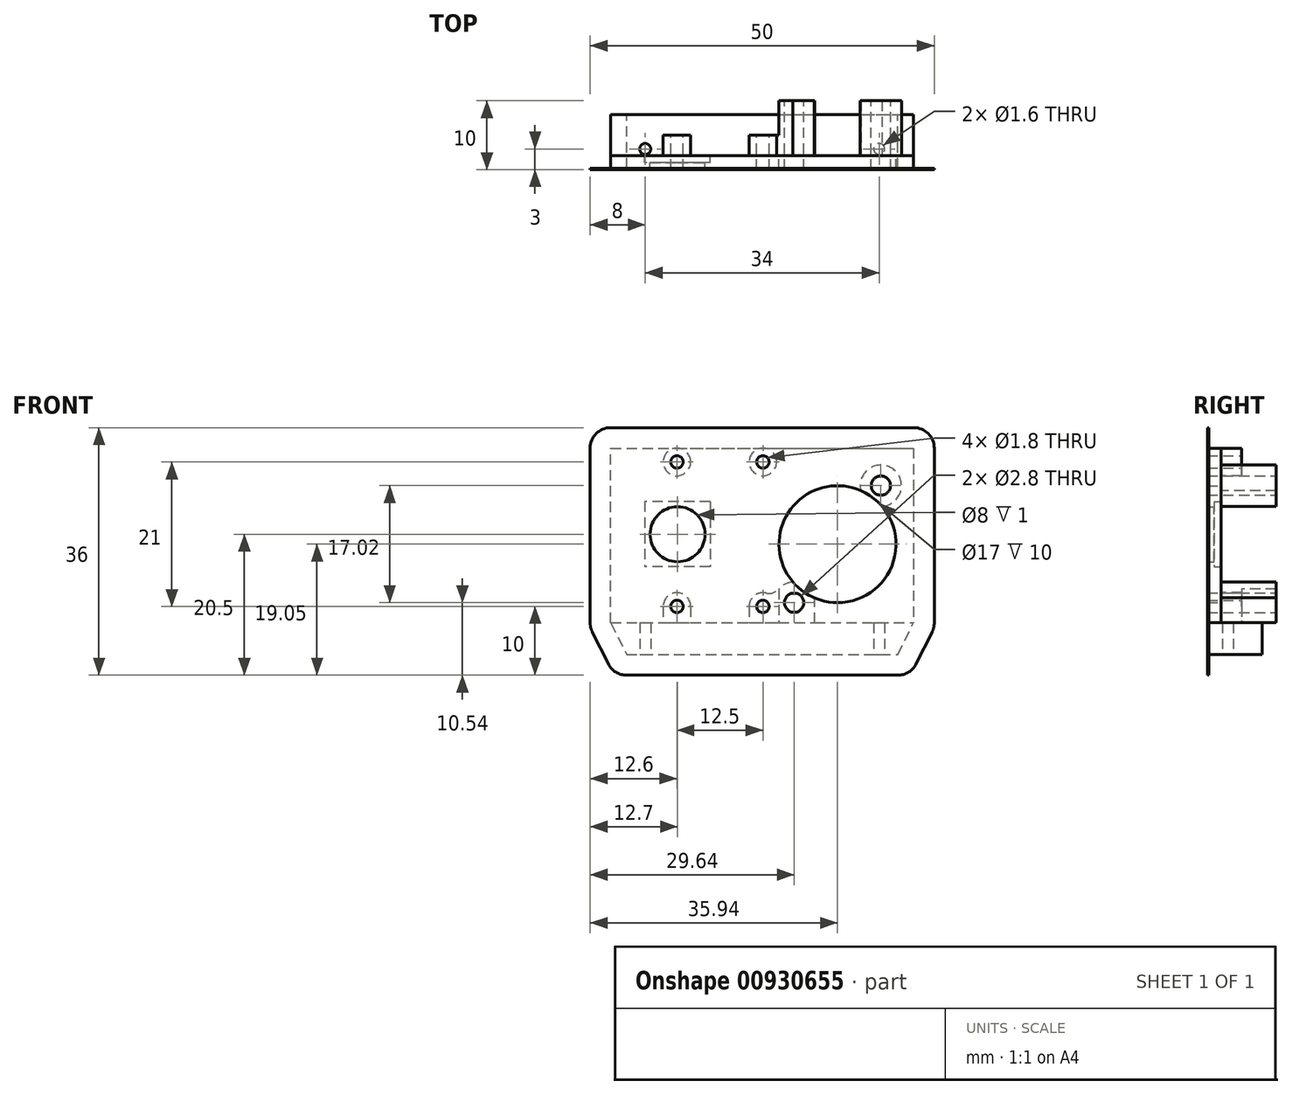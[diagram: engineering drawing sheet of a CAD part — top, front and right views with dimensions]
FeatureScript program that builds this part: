
annotation { "Feature Type Name" : "Feature", "Feature Type Description" : "" }
export const myFeature = defineFeature(function(context is Context, id is Id, definition is map)
    precondition{}
    {
        {
            var Q0;
            Q0=qCreatedBy(makeId("Front.planeOp"),FACE);
            var sketch = newSketch(context, id + "F0", { "sketchPlane" : qUnion([Q0])});
            skLineSegment(sketch, "E0", {"start": v(-22.5, 0) * mm, "end": v(22.5, 0) * mm, "construction": true});
            skLineSegment(sketch, "E1", {"start": v(-20, -5) * mm, "end": v(20, -5) * mm, "construction": true});
            skLineSegment(sketch, "E2", {"start": v(20, -5) * mm, "end": v(22.5, 0) * mm, "construction": true});
            skLineSegment(sketch, "E3", {"start": v(-22.5, 0) * mm, "end": v(-20, -5) * mm, "construction": true});
            skLineSegment(sketch, "E4.bottom", {"start": v(2.1, 22.6) * mm, "end": v(22, 22.6) * mm, "construction": true});
            skLineSegment(sketch, "E4.top", {"start": v(2.1, 0.5) * mm, "end": v(22, 0.5) * mm, "construction": true});
            skLineSegment(sketch, "E4.left", {"start": v(2.1, 22.6) * mm, "end": v(2.1, 0.5) * mm, "construction": true});
            skLineSegment(sketch, "E4.right", {"start": v(22, 22.6) * mm, "end": v(22, 0.5) * mm, "construction": true});
            skLineSegment(sketch, "E5.bottom", {"start": v(-19.76, 25.5) * mm, "end": v(0.1, 25.5) * mm, "construction": true});
            skLineSegment(sketch, "E5.top", {"start": v(-19.76, 0.5) * mm, "end": v(0.1, 0.5) * mm, "construction": true});
            skLineSegment(sketch, "E5.left", {"start": v(-21.76, 23.5) * mm, "end": v(-21.76, 2.5) * mm, "construction": true});
            skLineSegment(sketch, "E5.right", {"start": v(2.1, 23.5) * mm, "end": v(2.1, 2.5) * mm, "construction": true});
            skArc(sketch, "E6", {"start": v(-19.76, 25.5) * mm, "mid": v(-21.18, 24.91) * mm, "end": v(-21.76, 23.5) * mm, "construction": true});
            skArc(sketch, "E7", {"start": v(2.1, 23.5) * mm, "mid": v(1.51, 24.91) * mm, "end": v(0.1, 25.5) * mm, "construction": true});
            skArc(sketch, "E8", {"start": v(-21.76, 2.5) * mm, "mid": v(-21.18, 1.09) * mm, "end": v(-19.76, 0.5) * mm, "construction": true});
            skArc(sketch, "E9", {"start": v(0.1, 0.5) * mm, "mid": v(1.51, 1.09) * mm, "end": v(2.1, 2.5) * mm, "construction": true});
            skCircle(sketch, "E10", {"center": v(-12.4, 23.5) * mm, "radius": 1.1 * mm, "construction": true});
            skCircle(sketch, "E11", {"center": v(-12.4, 2.5) * mm, "radius": 1.1 * mm, "construction": true});
            skCircle(sketch, "E12", {"center": v(0.1, 2.5) * mm, "radius": 1.1 * mm, "construction": true});
            skCircle(sketch, "E13", {"center": v(0.1, 23.5) * mm, "radius": 1.1 * mm, "construction": true});
            skLineSegment(sketch, "E14", {"start": v(-12.4, 23.5) * mm, "end": v(0.1, 23.5) * mm, "construction": true});
            skLineSegment(sketch, "E15", {"start": v(-12.4, 23.5) * mm, "end": v(-12.4, 2.5) * mm, "construction": true});
            skCircle(sketch, "E16", {"center": v(10.94, 11.55) * mm, "radius": 8.2 * mm, "construction": true});
            skCircle(sketch, "E17", {"center": v(17.24, 20.06) * mm, "radius": 1.55 * mm, "construction": true});
            skCircle(sketch, "E18", {"center": v(4.64, 3.04) * mm, "radius": 1.55 * mm, "construction": true});
            skLineSegment(sketch, "E19.bottom", {"start": v(-16.55, 17.25) * mm, "end": v(-8.05, 17.25) * mm, "construction": true});
            skLineSegment(sketch, "E19.top", {"start": v(-16.55, 8.75) * mm, "end": v(-8.05, 8.75) * mm, "construction": true});
            skLineSegment(sketch, "E19.left", {"start": v(-16.55, 17.25) * mm, "end": v(-16.55, 8.75) * mm, "construction": true});
            skLineSegment(sketch, "E19.right", {"start": v(-8.05, 17.25) * mm, "end": v(-8.05, 8.75) * mm, "construction": true});
            skCircle(sketch, "E20", {"center": v(-12.3, 13) * mm, "radius": 3.7 * mm, "construction": true});
            skCircle(sketch, "E21", {"center": v(20.8, 17.44) * mm, "radius": 0.5 * mm, "construction": true});
            skCircle(sketch, "E22", {"center": v(20.8, 14.9) * mm, "radius": 0.5 * mm, "construction": true});
            skLineSegment(sketch, "E23", {"start": v(20.8, 17.44) * mm, "end": v(20.8, 2.2) * mm, "construction": true});
            skCircle(sketch, "E24", {"center": v(20.8, 12.36) * mm, "radius": 0.5 * mm, "construction": true});
            skCircle(sketch, "E25", {"center": v(20.8, 9.82) * mm, "radius": 0.5 * mm, "construction": true});
            skCircle(sketch, "E26", {"center": v(20.8, 7.28) * mm, "radius": 0.5 * mm, "construction": true});
            skCircle(sketch, "E27", {"center": v(20.8, 4.74) * mm, "radius": 0.5 * mm, "construction": true});
            skCircle(sketch, "E28", {"center": v(20.8, 2.2) * mm, "radius": 0.5 * mm, "construction": true});
            skSolve(sketch);
        }
        {
            var Q0;
            Q0=qCreatedBy(makeId("Front.planeOp"),FACE);
            var sketch = newSketch(context, id + "F1", { "sketchPlane" : qUnion([Q0])});
            skLineSegment(sketch, "E29", {"start": v(-22, 0.12) * mm, "end": v(-19.7, -4.5) * mm});
            skLineSegment(sketch, "E30", {"start": v(-19.7, -4.5) * mm, "end": v(19.7, -4.5) * mm});
            skLineSegment(sketch, "E31", {"start": v(19.7, -4.5) * mm, "end": v(22, 0.12) * mm});
            skLineSegment(sketch, "E32", {"start": v(-22, 0.12) * mm, "end": v(-22, 25.5) * mm});
            skLineSegment(sketch, "E33", {"start": v(-22, 25.5) * mm, "end": v(22, 25.5) * mm});
            skLineSegment(sketch, "E34", {"start": v(22, 25.5) * mm, "end": v(22, 0.12) * mm});
            skCircle(sketch, "E35", {"center": v(-12.3, 13) * mm, "radius": 4 * mm});
            skCircle(sketch, "E36", {"center": v(10.94, 11.55) * mm, "radius": 8.5 * mm});
            skSolve(sketch);
        }
        {
            var Q0;
            Q0=qSketchRegion(id+"F1",true);
            extrude(context, id + "F2", {"entities" : qUnion([Q0]), "depth" : 2 * mm, "offsetDistance" : 25 * mm});
        }
        {
            var Q0;
            Q0=makeQuery(id+"F2.opExtrude","CAP_FACE",FACE,{"disambiguationData":[OSD([sQuery(id+"F1.wireOp",EDGE,"E29"),sQuery(id+"F1.wireOp",EDGE,"E30"),sQuery(id+"F1.wireOp",EDGE,"E31"),sQuery(id+"F1.wireOp",EDGE,"E32"),sQuery(id+"F1.wireOp",EDGE,"E33"),sQuery(id+"F1.wireOp",EDGE,"E34"),sQuery(id+"F1.wireOp",EDGE,"E35"),sQuery(id+"F1.wireOp",EDGE,"E36")])],"isStart":true});
            var sketch = newSketch(context, id + "F3", { "sketchPlane" : qUnion([Q0])});
            skLineSegment(sketch, "E37", {"start": v(-22, 0.12) * mm, "end": v(-19.7, -4.5) * mm});
            skLineSegment(sketch, "E38", {"start": v(-19.7, -4.5) * mm, "end": v(19.7, -4.5) * mm});
            skLineSegment(sketch, "E39", {"start": v(19.7, -4.5) * mm, "end": v(22, 0.12) * mm});
            skLineSegment(sketch, "E40", {"start": v(22, 0.12) * mm, "end": v(-22, 0.12) * mm});
            skSolve(sketch);
        }
        {
            var Q0;
            Q0=qSketchRegion(id+"F3",true);
            extrude(context, id + "F4", {"entities" : qUnion([Q0]), "operationType" : NewBodyOperationType.ADD, "depth" : 6 * mm, "offsetDistance" : 25 * mm});
        }
        {
            var Q0;
            Q0=makeQuery(id+"F4.boolean.opBoolean","MERGE",FACE,{"derivedFrom":[makeQuery(id+"F2.opExtrude","SWEPT_FACE",FACE,{"disambiguationData":[OSD([sQuery(id+"F1.wireOp",EDGE,"E30")])]}),makeQuery(id+"F4.opExtrude","SWEPT_FACE",FACE,{"disambiguationData":[OSD([sQuery(id+"F3.wireOp",EDGE,"E38")])]})]});
            var sketch = newSketch(context, id + "F5", { "sketchPlane" : qUnion([Q0])});
            skCircle(sketch, "E41", {"center": v(-17, -1) * mm, "radius": 0.8 * mm});
            skCircle(sketch, "E42", {"center": v(17, -1) * mm, "radius": 0.8 * mm});
            skSolve(sketch);
        }
        {
            var Q0;
            Q0=qSketchRegion(id+"F5",true);
            extrude(context, id + "F6", {"entities" : qUnion([Q0]), "operationType" : NewBodyOperationType.REMOVE, "endBound" : BoundingType.UP_TO_NEXT, "oppositeDirection" : true, "depth" : 25 * mm, "offsetDistance" : 25 * mm});
        }
        {
            var Q0;
            Q0=makeQuery(id+"F2.opExtrude","CAP_FACE",FACE,{"disambiguationData":[OSD([sQuery(id+"F1.wireOp",EDGE,"E29"),sQuery(id+"F1.wireOp",EDGE,"E30"),sQuery(id+"F1.wireOp",EDGE,"E31"),sQuery(id+"F1.wireOp",EDGE,"E32"),sQuery(id+"F1.wireOp",EDGE,"E33"),sQuery(id+"F1.wireOp",EDGE,"E34"),sQuery(id+"F1.wireOp",EDGE,"E35"),sQuery(id+"F1.wireOp",EDGE,"E36")])],"isStart":true});
            var sketch = newSketch(context, id + "F7", { "sketchPlane" : qUnion([Q0])});
            skArc(sketch, "E43", {"start": v(-14.33, 19.35) * mm, "mid": v(-19.03, 22.47) * mm, "end": v(-17.4, 17.06) * mm});
            skArc(sketch, "E44", {"start": v(-7.55, 3.75) * mm, "mid": v(-7.62, 3.4) * mm, "end": v(-7.64, 3.04) * mm});
            skArc(sketch, "E45", {"start": v(-14.33, 19.35) * mm, "mid": v(-16, 18.38) * mm, "end": v(-17.4, 17.06) * mm});
            skArc(sketch, "E46", {"start": v(-7.55, 3.75) * mm, "mid": v(-5.88, 4.72) * mm, "end": v(-4.47, 6.04) * mm});
            skLineSegment(sketch, "E47", {"start": v(-2.4, 5.04) * mm, "end": v(-2.4, 0.12) * mm});
            skLineSegment(sketch, "E48", {"start": v(-7.64, 0.12) * mm, "end": v(-2.4, 0.12) * mm});
            skLineSegment(sketch, "E49", {"start": v(-7.64, 0.12) * mm, "end": v(-7.64, 3.04) * mm});
            skArc(sketch, "E50.trimOffspring", {"start": v(-2.4, 5.04) * mm, "mid": v(-3.34, 5.74) * mm, "end": v(-4.47, 6.04) * mm});
            skSolve(sketch);
        }
        {
            var Q0;
            Q0=qSketchRegion(id+"F7",true);
            extrude(context, id + "F8", {"entities" : qUnion([Q0]), "operationType" : NewBodyOperationType.ADD, "depth" : 8 * mm, "offsetDistance" : 25 * mm});
        }
        {
            var Q0;
            Q0=makeQuery(id+"F8.opExtrude","CAP_FACE",FACE,{"disambiguationData":[OSD([sQuery(id+"F7.wireOp",EDGE,"E43"),sQuery(id+"F7.wireOp",EDGE,"E45")])],"isStart":false});
            var sketch = newSketch(context, id + "F9", { "sketchPlane" : qUnion([Q0])});
            skCircle(sketch, "E51", {"center": v(-17.24, 20.06) * mm, "radius": 1.4 * mm});
            skCircle(sketch, "E52", {"center": v(-4.64, 3.04) * mm, "radius": 1.4 * mm});
            skSolve(sketch);
        }
        {
            var Q0;
            Q0=qSketchRegion(id+"F9",true);
            extrude(context, id + "F10", {"entities" : qUnion([Q0]), "operationType" : NewBodyOperationType.REMOVE, "endBound" : BoundingType.UP_TO_NEXT, "oppositeDirection" : true, "depth" : 25 * mm, "offsetDistance" : 25 * mm});
        }
        {
            var Q0;
            Q0=makeQuery(id+"F2.opExtrude","CAP_FACE",FACE,{"disambiguationData":[OSD([sQuery(id+"F1.wireOp",EDGE,"E29"),sQuery(id+"F1.wireOp",EDGE,"E30"),sQuery(id+"F1.wireOp",EDGE,"E31"),sQuery(id+"F1.wireOp",EDGE,"E32"),sQuery(id+"F1.wireOp",EDGE,"E33"),sQuery(id+"F1.wireOp",EDGE,"E34"),sQuery(id+"F1.wireOp",EDGE,"E35"),sQuery(id+"F1.wireOp",EDGE,"E36")])],"isStart":true});
            var sketch = newSketch(context, id + "F11", { "sketchPlane" : qUnion([Q0])});
            skCircle(sketch, "E53", {"center": v(-0.1, 23.5) * mm, "radius": 2 * mm});
            skCircle(sketch, "E54", {"center": v(12.4, 23.5) * mm, "radius": 2 * mm});
            skArc(sketch, "E55", {"start": v(1.9, 2.5) * mm, "mid": v(1.14, 4.07) * mm, "end": v(-0.55, 4.45) * mm});
            skArc(sketch, "E56", {"start": v(14.4, 2.5) * mm, "mid": v(12.4, 4.5) * mm, "end": v(10.4, 2.5) * mm});
            skLineSegment(sketch, "E57", {"start": v(1.9, 2.5) * mm, "end": v(1.9, 0.12) * mm});
            skLineSegment(sketch, "E58", {"start": v(-2.4, 0.12) * mm, "end": v(1.9, 0.12) * mm});
            skLineSegment(sketch, "E59", {"start": v(10.4, 2.5) * mm, "end": v(10.4, 0.12) * mm});
            skLineSegment(sketch, "E60", {"start": v(14.4, 2.5) * mm, "end": v(14.4, 0.12) * mm});
            skLineSegment(sketch, "E61", {"start": v(10.4, 0.12) * mm, "end": v(14.4, 0.12) * mm});
            skArc(sketch, "E62", {"start": v(-2.4, 5.04) * mm, "mid": v(-1.56, 4.49) * mm, "end": v(-0.55, 4.45) * mm});
            skLineSegment(sketch, "E63", {"start": v(-2.4, 5.04) * mm, "end": v(-2.4, 0.12) * mm});
            skSolve(sketch);
        }
        {
            var Q0;
            Q0=qSketchRegion(id+"F11",true);
            extrude(context, id + "F12", {"entities" : qUnion([Q0]), "operationType" : NewBodyOperationType.ADD, "depth" : 3 * mm, "offsetDistance" : 25 * mm});
        }
        {
            var Q0;
            Q0=makeQuery(id+"F2.opExtrude","CAP_FACE",FACE,{"disambiguationData":[OSD([sQuery(id+"F1.wireOp",EDGE,"E29"),sQuery(id+"F1.wireOp",EDGE,"E30"),sQuery(id+"F1.wireOp",EDGE,"E31"),sQuery(id+"F1.wireOp",EDGE,"E32"),sQuery(id+"F1.wireOp",EDGE,"E33"),sQuery(id+"F1.wireOp",EDGE,"E34"),sQuery(id+"F1.wireOp",EDGE,"E35"),sQuery(id+"F1.wireOp",EDGE,"E36")])],"isStart":true});
            var sketch = newSketch(context, id + "F13", { "sketchPlane" : qUnion([Q0])});
            skLineSegment(sketch, "E64.bottom", {"start": v(7.55, 17.75) * mm, "end": v(17.05, 17.75) * mm});
            skLineSegment(sketch, "E64.top", {"start": v(7.55, 8.25) * mm, "end": v(17.05, 8.25) * mm});
            skLineSegment(sketch, "E64.left", {"start": v(7.55, 17.75) * mm, "end": v(7.55, 8.25) * mm});
            skLineSegment(sketch, "E64.right", {"start": v(17.05, 17.75) * mm, "end": v(17.05, 8.25) * mm});
            skCircle(sketch, "E65", {"center": v(12.3, 13) * mm, "radius": 4 * mm});
            skSolve(sketch);
        }
        {
            var Q0;
            Q0=qSketchRegion(id+"F13",true);
            extrude(context, id + "F14", {"entities" : qUnion([Q0]), "operationType" : NewBodyOperationType.REMOVE, "oppositeDirection" : true, "depth" : 1 * mm, "offsetDistance" : 25 * mm});
        }
        {
            var Q0;
            Q0=makeQuery(id+"F12.opExtrude","CAP_FACE",FACE,{"disambiguationData":[OSD([sQuery(id+"F11.wireOp",EDGE,"E53")])],"isStart":false});
            var sketch = newSketch(context, id + "F15", { "sketchPlane" : qUnion([Q0])});
            skCircle(sketch, "E66", {"center": v(-0.1, 23.5) * mm, "radius": 0.9 * mm});
            skCircle(sketch, "E67", {"center": v(12.4, 23.5) * mm, "radius": 0.9 * mm});
            skCircle(sketch, "E68", {"center": v(-0.1, 2.5) * mm, "radius": 0.9 * mm});
            skCircle(sketch, "E69", {"center": v(12.4, 2.5) * mm, "radius": 0.9 * mm});
            skSolve(sketch);
        }
        {
            var Q0;
            Q0=qSketchRegion(id+"F15",true);
            extrude(context, id + "F16", {"entities" : qUnion([Q0]), "operationType" : NewBodyOperationType.REMOVE, "endBound" : BoundingType.UP_TO_NEXT, "oppositeDirection" : true, "depth" : 25 * mm, "offsetDistance" : 25 * mm});
        }
        {
            var Q0;
            Q0=makeQuery(id+"F2.opExtrude","CAP_FACE",FACE,{"disambiguationData":[OSD([sQuery(id+"F1.wireOp",EDGE,"E29"),sQuery(id+"F1.wireOp",EDGE,"E30"),sQuery(id+"F1.wireOp",EDGE,"E31"),sQuery(id+"F1.wireOp",EDGE,"E32"),sQuery(id+"F1.wireOp",EDGE,"E33"),sQuery(id+"F1.wireOp",EDGE,"E34"),sQuery(id+"F1.wireOp",EDGE,"E35"),sQuery(id+"F1.wireOp",EDGE,"E36")])],"isStart":false});
            var sketch = newSketch(context, id + "F17", { "sketchPlane" : qUnion([Q0])});
            skLineSegment(sketch, "E70", {"start": v(-22, 25.5) * mm, "end": v(-22, 0.12) * mm});
            skLineSegment(sketch, "E71", {"start": v(-22, 0.12) * mm, "end": v(-19.7, -4.5) * mm});
            skLineSegment(sketch, "E72", {"start": v(-19.7, -4.5) * mm, "end": v(19.7, -4.5) * mm});
            skLineSegment(sketch, "E73", {"start": v(19.7, -4.5) * mm, "end": v(22, 0.12) * mm});
            skLineSegment(sketch, "E74", {"start": v(22, 0.12) * mm, "end": v(22, 25.5) * mm});
            skLineSegment(sketch, "E75", {"start": v(22, 25.5) * mm, "end": v(-22, 25.5) * mm});
            skLineSegment(sketch, "E76", {"start": v(-25, 25.5) * mm, "end": v(-25, 0.12) * mm});
            skLineSegment(sketch, "E77", {"start": v(-22, 28.5) * mm, "end": v(22, 28.5) * mm});
            skLineSegment(sketch, "E78", {"start": v(25, 25.5) * mm, "end": v(25, 0.12) * mm});
            skLineSegment(sketch, "E79", {"start": v(-24.68, -1.22) * mm, "end": v(-22.37, -5.84) * mm});
            skLineSegment(sketch, "E80", {"start": v(-19.7, -7.5) * mm, "end": v(19.7, -7.5) * mm});
            skLineSegment(sketch, "E81", {"start": v(24.68, -1.22) * mm, "end": v(22.37, -5.84) * mm});
            skArc(sketch, "E82", {"start": v(-22, 28.5) * mm, "mid": v(-24.12, 27.62) * mm, "end": v(-25, 25.5) * mm});
            skArc(sketch, "E83", {"start": v(25, 25.5) * mm, "mid": v(24.12, 27.62) * mm, "end": v(22, 28.5) * mm});
            skArc(sketch, "E84", {"start": v(24.68, -1.22) * mm, "mid": v(24.92, -0.57) * mm, "end": v(25, 0.12) * mm});
            skArc(sketch, "E85", {"start": v(19.7, -7.5) * mm, "mid": v(21.27, -7.05) * mm, "end": v(22.37, -5.84) * mm});
            skArc(sketch, "E86", {"start": v(-25, 0.12) * mm, "mid": v(-24.92, -0.57) * mm, "end": v(-24.68, -1.22) * mm});
            skArc(sketch, "E87", {"start": v(-22.37, -5.84) * mm, "mid": v(-21.27, -7.05) * mm, "end": v(-19.7, -7.5) * mm});
            skSolve(sketch);
        }
        {
            var Q0;
            Q0=qSketchRegion(id+"F17",true);
            extrude(context, id + "F18", {"entities" : qUnion([Q0]), "operationType" : NewBodyOperationType.ADD, "oppositeDirection" : true, "depth" : 0.2 * mm, "offsetDistance" : 25 * mm});
        }
    });
